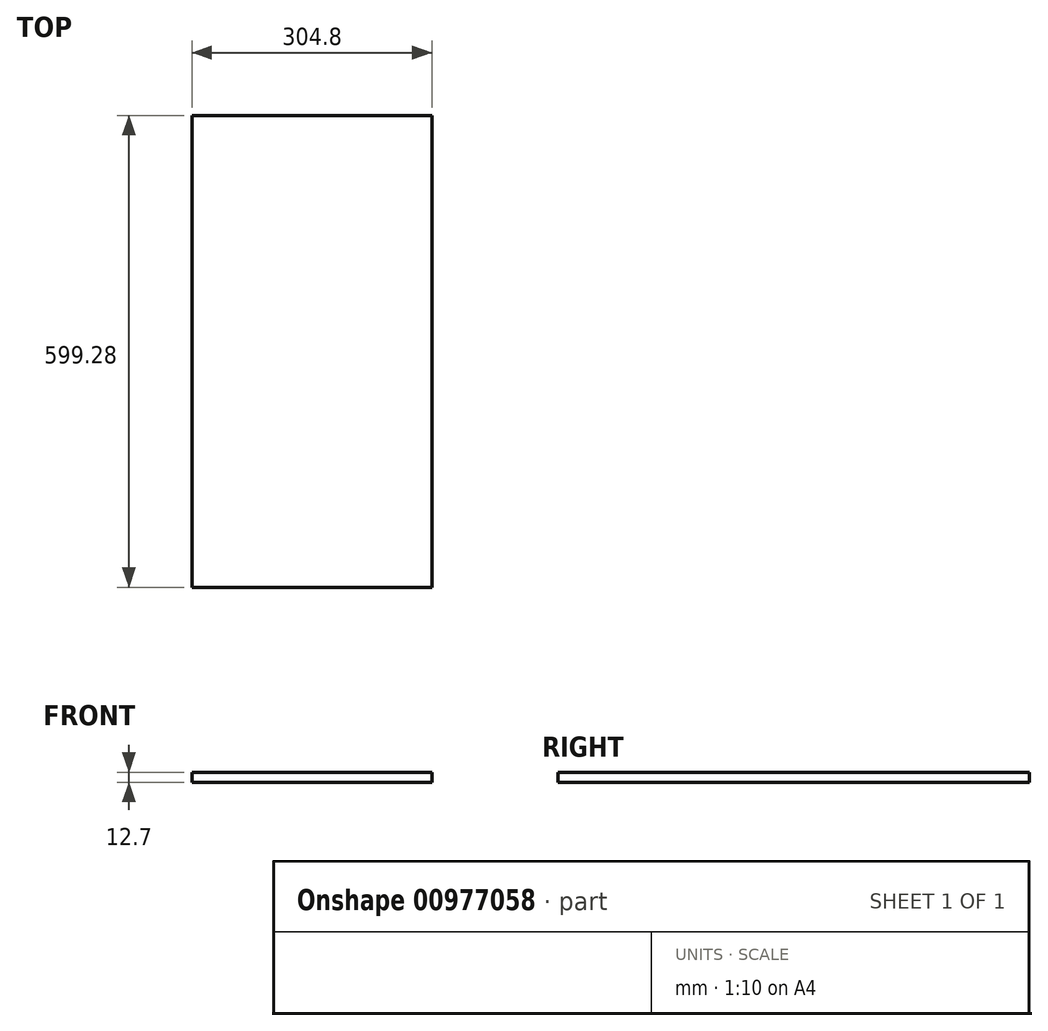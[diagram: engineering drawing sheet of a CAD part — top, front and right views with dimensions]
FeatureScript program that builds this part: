
annotation { "Feature Type Name" : "Feature", "Feature Type Description" : "" }
export const myFeature = defineFeature(function(context is Context, id is Id, definition is map)
    precondition{}
    {
        {
            var Q0;
            Q0=qCreatedBy(makeId("Front.planeOp"),FACE);
            var sketch = newSketch(context, id + "F0", { "sketchPlane" : qUnion([Q0])});
            skLineSegment(sketch, "E0.bottom", {"start": v(152.4, -6.35) * mm, "end": v(-152.4, -6.35) * mm});
            skLineSegment(sketch, "E0.top", {"start": v(152.4, 6.35) * mm, "end": v(-152.4, 6.35) * mm});
            skLineSegment(sketch, "E0.left", {"start": v(152.4, -6.35) * mm, "end": v(152.4, 6.35) * mm});
            skLineSegment(sketch, "E0.right", {"start": v(-152.4, -6.35) * mm, "end": v(-152.4, 6.35) * mm});
            skPoint(sketch, "E0.middle", {"position": v(0, 0) * mm});
            skSolve(sketch);
        }
        {
            var Q0;
            Q0 = qSketchRegion(id + "F0", true);
            extrude(context, id + "F1", {"entities" : qUnion([Q0]), "endBound" : BoundingType.SYMMETRIC, "depth" : 599.3 * mm, "offsetDistance" : 25.4 * mm});
        }
    });
